# Revit family: Lochplatte
name_source: partatom
category: HLS-Bauteile
revit_build: Autodesk Revit 2017 (Build: 20190507_1515(x64)
units: mm (PartAtom-declared; Revit-internal decimal feet)

## family parameters
Arbeitsebenenbasiert = Ja
Beim Laden mit Abzugskörper schneiden = Nein
Bemaßung runder Anschluss = Durchmesser verwenden
Gemeinsam genutzt = Ja
Immer vertikal = Nein
Raumberechnungspunkt = Nein
Teiletyp = Normal

## types (3) — shared parameters
Anzugsmoment = 0.00 kN-m
B = 40 mm  [stored 0.131234 ft]
Breite = 40 mm  [stored 0.131234 ft]
Fabrikat = MEFA
Firma = MEFA Befestigungs- und Montagesysteme GmbH
Kurztext1 = Lochplatte C-Profil 45
L = 45 mm  [stored 0.147638 ft]
Länge = 45 mm  [stored 0.147638 ft]
Material = Stahl
Materialname = S235
Profiltyp = 45
S = 6 mm  [stored 0.019685 ft]
Vorgabe-Ansicht = 1219 mm
zero-valued in all types: Stärke Material

## per-type parameters (varying)
| type | Artikelnummer | EAN | Gewicht | Gewicht pro Bauteil | Kurztext2 | Lochdurchmesser | Mengeneinheit | Oberflaeche | Stärke | d2 | für Gewinde | vpe |
| Lochplatte 17 | 0814017 | 4250928419736 | 0.08 kg | 0.08 kg | Bohrung 17 mm 45x40x6 mm | 17 mm | St | galvanisch verzinkt | 6 mm  [stored 0.019685 ft] | 9 mm  [stored 0.0295276 ft] | M16 | 50 |
| Lochplatte 13 | 0814016 | 4250928419729 | 0.08 kg | 0.08 kg | Bohrung 13 mm 45x40x6 mm | 13 mm | St | galvanisch verzinkt | 6 mm  [stored 0.019685 ft] | 7 mm  [stored 0.0229659 ft] | M12 | 50 |
| Lochplatte 13 fvz | 0814016/fvz |  | 0.00 kg | 0.00 kg | Bohrung 13 mm 45x40x6 mm |  |  |  | 0 mm  [stored 0 ft] | 7 mm  [stored 0.0229659 ft] |  |  |

note: [stored X ft] marks values corroborated as IEEE doubles in the binary element streams (Revit-internal decimal feet)
